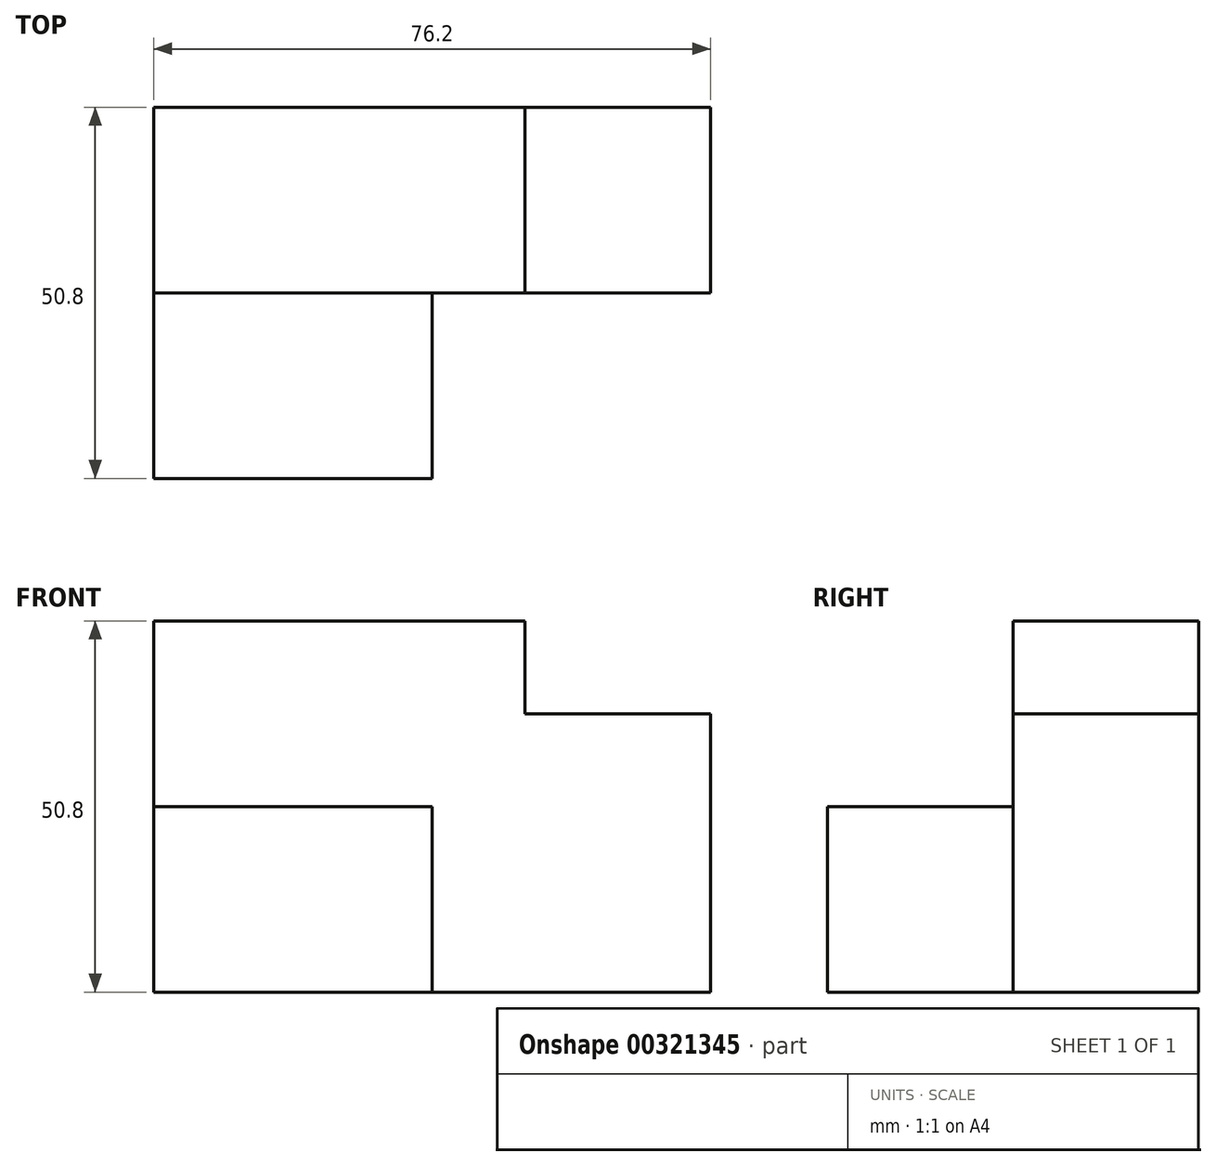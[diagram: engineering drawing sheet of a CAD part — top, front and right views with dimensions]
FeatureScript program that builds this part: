
annotation { "Feature Type Name" : "Feature", "Feature Type Description" : "" }
export const myFeature = defineFeature(function(context is Context, id is Id, definition is map)
    precondition{}
    {
        {
            var Q0;
            Q0=qCreatedBy(makeId("Front.planeOp"),FACE);
            var sketch = newSketch(context, id + "F0", { "sketchPlane" : qUnion([Q0])});
            skLineSegment(sketch, "E0.bottom", {"start": v(-35.31, 29.47) * mm, "end": v(40.89, 29.47) * mm});
            skLineSegment(sketch, "E0.top", {"start": v(-35.31, -21.33) * mm, "end": v(40.89, -21.33) * mm});
            skLineSegment(sketch, "E0.left", {"start": v(-35.31, 29.47) * mm, "end": v(-35.31, -21.33) * mm});
            skLineSegment(sketch, "E0.right", {"start": v(40.89, 29.47) * mm, "end": v(40.89, -21.33) * mm});
            skSolve(sketch);
        }
        {
            var Q0;
            Q0=makeQuery(id+"F0.imprint","IMPRINT",FACE,{"disambiguationData":[TD([[makeQuery(id+"F0.imprint","IMPRINT",EDGE,{"derivedFrom":sQuery(id+"F0.wireOp",EDGE,"E0.bottom")}),-1.0]])]});
            extrude(context, id + "F1", {"entities" : qUnion([Q0]), "depth" : 25.4 * mm});
        }
        {
            var Q0;
            Q0=makeQuery(id+"F1.opExtrude","CAP_FACE",FACE,{"disambiguationData":[OSD([sQuery(id+"F0.wireOp",EDGE,"E0.bottom"),sQuery(id+"F0.wireOp",EDGE,"E0.top"),sQuery(id+"F0.wireOp",EDGE,"E0.left"),sQuery(id+"F0.wireOp",EDGE,"E0.right")])],"isStart":false});
            var sketch = newSketch(context, id + "F2", { "sketchPlane" : qUnion([Q0])});
            skLineSegment(sketch, "E1.bottom", {"start": v(40.89, 29.47) * mm, "end": v(15.49, 29.47) * mm});
            skLineSegment(sketch, "E1.top", {"start": v(40.89, 16.77) * mm, "end": v(15.49, 16.77) * mm});
            skLineSegment(sketch, "E1.left", {"start": v(40.89, 29.47) * mm, "end": v(40.89, 16.77) * mm});
            skLineSegment(sketch, "E1.right", {"start": v(15.49, 29.47) * mm, "end": v(15.49, 16.77) * mm});
            skSolve(sketch);
        }
        {
            var Q0;
            Q0 = qSketchRegion(id + "F2", true);
            extrude(context, id + "F3", {"entities" : qUnion([Q0]), "operationType" : NewBodyOperationType.REMOVE, "oppositeDirection" : true, "depth" : 25.4 * mm});
        }
        {
            var Q0;
            Q0=makeQuery(id+"F1.opExtrude","CAP_FACE",FACE,{"disambiguationData":[OSD([sQuery(id+"F0.wireOp",EDGE,"E0.bottom"),sQuery(id+"F0.wireOp",EDGE,"E0.top"),sQuery(id+"F0.wireOp",EDGE,"E0.left"),sQuery(id+"F0.wireOp",EDGE,"E0.right")])],"isStart":false});
            var sketch = newSketch(context, id + "F4", { "sketchPlane" : qUnion([Q0])});
            skLineSegment(sketch, "E2.bottom", {"start": v(-35.31, -21.33) * mm, "end": v(2.79, -21.33) * mm});
            skLineSegment(sketch, "E2.top", {"start": v(-35.31, 4.07) * mm, "end": v(2.79, 4.07) * mm});
            skLineSegment(sketch, "E2.left", {"start": v(-35.31, -21.33) * mm, "end": v(-35.31, 4.07) * mm});
            skLineSegment(sketch, "E2.right", {"start": v(2.79, -21.33) * mm, "end": v(2.79, 4.07) * mm});
            skSolve(sketch);
        }
        {
            var Q0;
            Q0=makeQuery(id+"F4.imprint","IMPRINT",FACE,{"disambiguationData":[TD([[makeQuery(id+"F4.imprint","IMPRINT",EDGE,{"derivedFrom":sQuery(id+"F4.wireOp",EDGE,"E2.bottom")}),1.0]])]});
            extrude(context, id + "F5", {"entities" : qUnion([Q0]), "operationType" : NewBodyOperationType.ADD, "depth" : 25.4 * mm});
        }
    });
